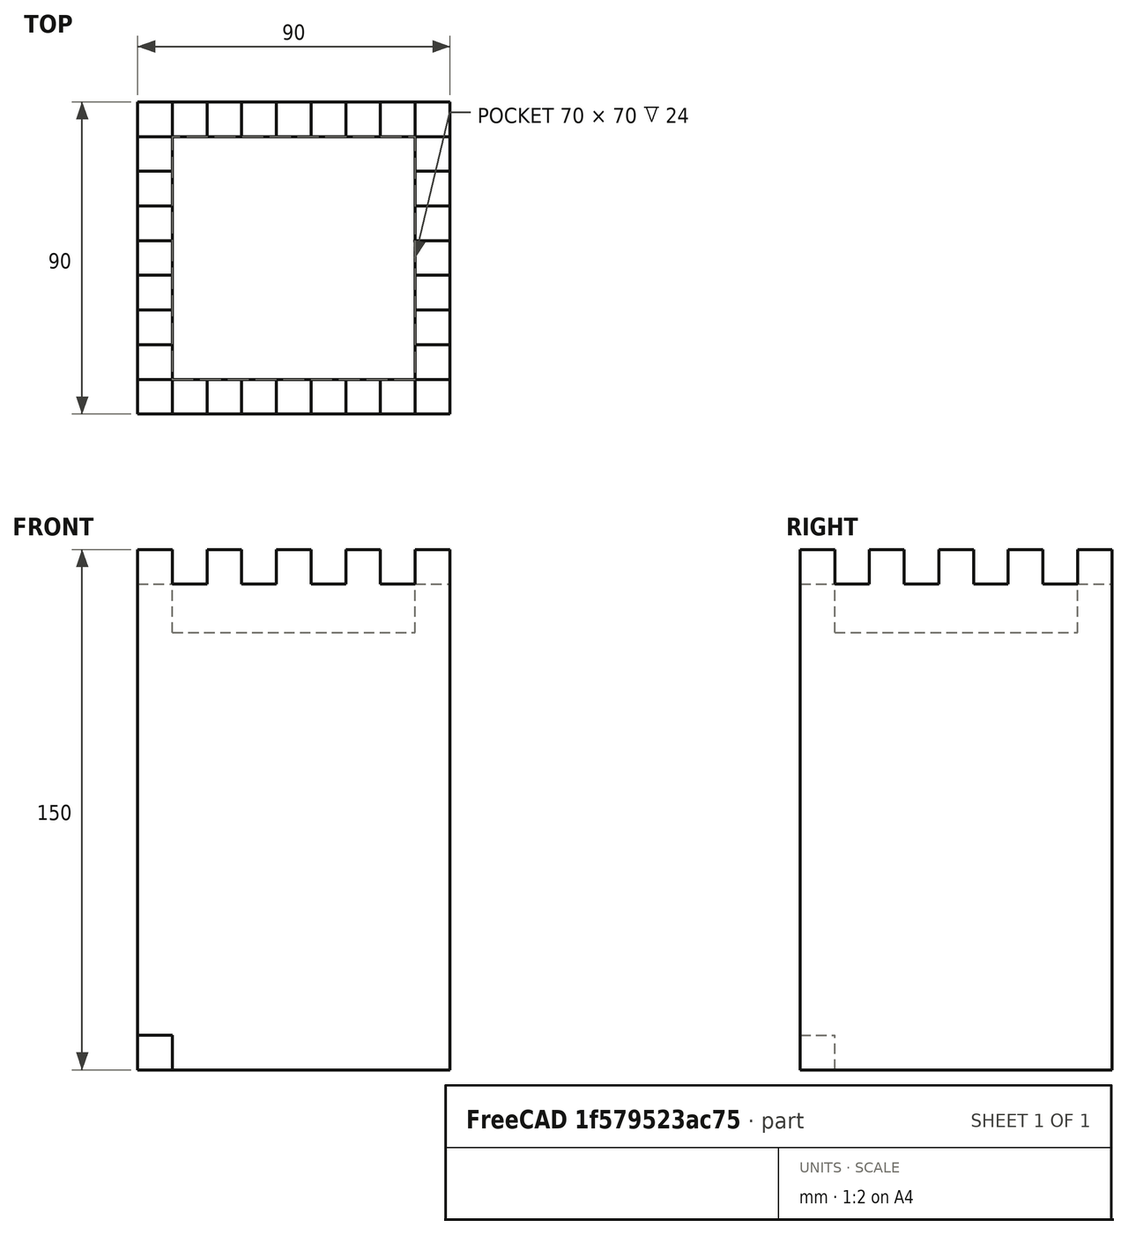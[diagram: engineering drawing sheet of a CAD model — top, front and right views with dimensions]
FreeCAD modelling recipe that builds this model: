
FCSTD DOCUMENT  (FreeCAD 1.0R39319 (Git))
Label: ojt1_t10r02_tower
License: All rights reserved
LicenseURL: https://en.wikipedia.org/wiki/All_rights_reserved
objects: Part::Box×4, Part::Cut×3, Part::FeaturePython×1
note: 7 computed .brp shape members not serialized (recipe doc carries the construction recipe); baked Part::Feature solids carry a one-line shape summary decoded from their .brp

FEATURE [Part::Box] Box  label="Cub"
  AttacherType = Attacher::AttachEngine3D
  Height = 150
  Length = 90
  Width = 90
FEATURE [Part::Box] Box001  label="Cub001"
  AttacherType = Attacher::AttachEngine3D
  Height = 10
  Length = 10
  Width = 10
FEATURE [Part::FeaturePython] Array  # Draft array (typed FeaturePython)
  AlwaysSyncPlacement = false
  Angle = 360
  ArrayType = 0
  Axis = (0,0,1)
  Base = -> Box001
  Center = (0,0,0)
  Count = 25
  ExpandArray = false
  Fuse = false
  IntervalAxis = (0,0,0)
  IntervalX = (20,0,0)
  IntervalY = (0,20,0)
  IntervalZ = (0,0,100)
  NumberCircles = 3
  NumberPolar = 5
  NumberX = 5
  NumberY = 5
  NumberZ = 1
  PlacementList = 25 placements: [(0,0,0),(0,20,0),(0,40,0),(0,60,0),(0,80,0),(20,0,0),(20,20,0),(20,40,0),(20,60,0),(20,80,0),(40,0,0),(40,20,0),(40,40,0),(40,60,0),(40,80,0),(60,0,0),(60,20,0),(60,40,0),(60,60,0),(60,80,0),(80,0,0),(80,20,0),(80,40,0),(80,60,0),(80,80,0)]
  RadialDistance = 50
  ScaleList = (25) [(1,1,1),(1,1,1),(1,1,1),(1,1,1),(1,1,1),(1,1,1),(1,1,1),(1,1,1),(1,1,1),(1,1,1),(1,1,1),(1,1,1),(1,1,1),(1,1,1),(1,1,1),(1,1,1),(1,1,1),(1,1,1),+7 more]
  Symmetry = 1
  TangentialDistance = 25
FEATURE [Part::Box] Box002  label="Cub002"
  AttacherType = Attacher::AttachEngine3D
  Height = 10
  Length = 90
  Width = 90
FEATURE [Part::Cut] Cut
  Base = -> Box002
  Placement = pos=(0,0,140) rot=(0,0,1;0rad)
  Refine = true
  Tool = -> Array
FEATURE [Part::Cut] Cut001
  Base = -> Box
  Refine = true
  Tool = -> Cut
FEATURE [Part::Box] Box003  label="Cub003"
  AttacherType = Attacher::AttachEngine3D
  Height = 25
  Length = 70
  Placement = pos=(10,10,126) rot=(0,0,1;0rad)
  Width = 70
FEATURE [Part::Cut] Cut002
  Base = -> Cut001
  Refine = true
  Tool = -> Box003
